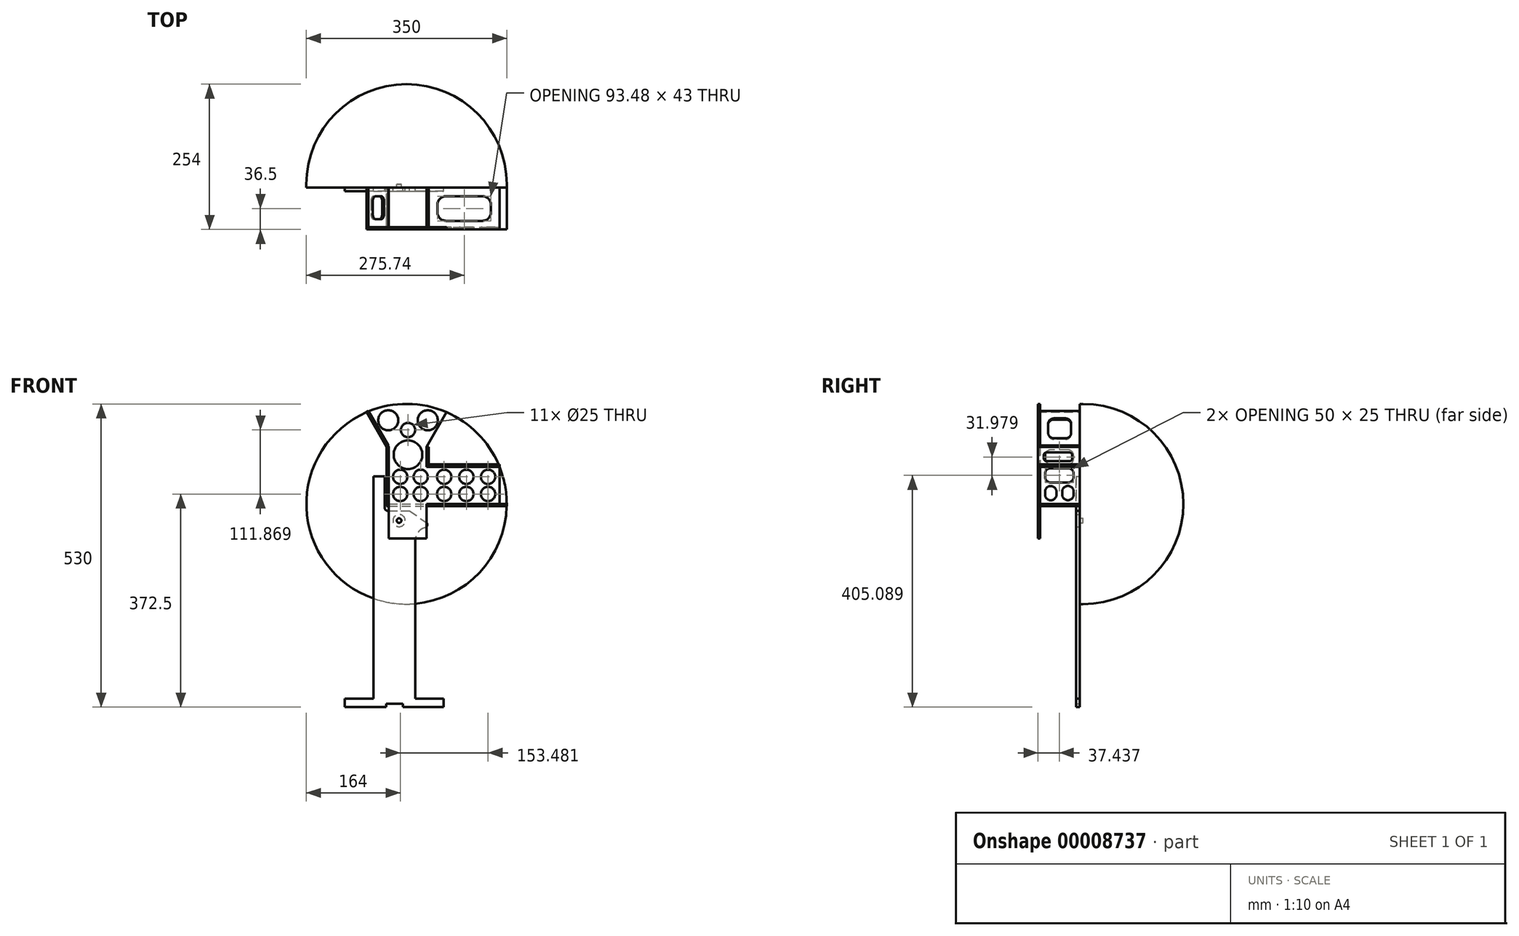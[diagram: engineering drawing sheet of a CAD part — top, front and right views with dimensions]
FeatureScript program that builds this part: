
annotation { "Feature Type Name" : "Feature", "Feature Type Description" : "" }
export const myFeature = defineFeature(function(context is Context, id is Id, definition is map)
    precondition{}
    {
        {
            var Q0;
            Q0=qCreatedBy(makeId("Right.planeOp"),FACE);
            cPlane(context, id + "F0", {"entities" : qUnion([Q0]), "cplaneType" : CPlaneType.OFFSET, "offset" : (70 / 2) * mm, "width" : 150 * mm, "height" : 150 * mm});
        }
        {
            var Q0;
            Q0=qCreatedBy(makeId("Front.planeOp"),FACE);
            var sketch = newSketch(context, id + "F1", { "sketchPlane" : qUnion([Q0])});
            skCircle(sketch, "E0", {"center": v(0, 0) * mm, "radius": 175 * mm});
            skCircle(sketch, "E1", {"center": v(-13, -29) * mm, "radius": 4 * mm});
            skSolve(sketch);
        }
        {
            var Q0;
            Q0 = qSketchRegion(id + "F1", true);
            extrude(context, id + "F2", {"entities" : qUnion([Q0]), "depth" : 6 * mm});
        }
        {
            var Q0;
            Q0=qCreatedBy(id+"F0.planeOp",FACE);
            var sketch = newSketch(context, id + "F3", { "sketchPlane" : qUnion([Q0])});
            skLineSegment(sketch, "E2.bottom", {"start": v(-6, 0) * mm, "end": v(-79, 0) * mm, "construction": true});
            skLineSegment(sketch, "E2.top", {"start": v(-6, 100) * mm, "end": v(-79, 100) * mm});
            skLineSegment(sketch, "E3", {"start": v(-79, 65) * mm, "end": v(-6, 65) * mm});
            skLineSegment(sketch, "E4", {"start": v(-79, 65) * mm, "end": v(-79, 0) * mm, "construction": true});
            skLineSegment(sketch, "E5", {"start": v(-79, 65) * mm, "end": v(-79, 100) * mm});
            skLineSegment(sketch, "E6", {"start": v(-6, 100) * mm, "end": v(-6, 65) * mm});
            skLineSegment(sketch, "E7", {"start": v(-6, 65) * mm, "end": v(-6, 0) * mm, "construction": true});
            skLineSegment(sketch, "E8.bottom", {"start": v(-64, 90) * mm, "end": v(-24, 90) * mm});
            skLineSegment(sketch, "E8.top", {"start": v(-64, 75) * mm, "end": v(-24, 75) * mm});
            skLineSegment(sketch, "E8.left", {"start": v(-69, 85) * mm, "end": v(-69, 80) * mm});
            skLineSegment(sketch, "E8.right", {"start": v(-19, 85) * mm, "end": v(-19, 80) * mm});
            skPoint(sketch, "E9.visualSharp", {"position": v(-69, 90) * mm});
            skArc(sketch, "E9.filletArc", {"start": v(-64, 90) * mm, "mid": v(-67.54, 88.54) * mm, "end": v(-69, 85) * mm});
            skPoint(sketch, "E10.visualSharp", {"position": v(-19, 90) * mm});
            skArc(sketch, "E10.filletArc", {"start": v(-19, 85) * mm, "mid": v(-20.46, 88.54) * mm, "end": v(-24, 90) * mm});
            skPoint(sketch, "E11.visualSharp", {"position": v(-19, 75) * mm});
            skArc(sketch, "E11.filletArc", {"start": v(-24, 75) * mm, "mid": v(-20.46, 76.46) * mm, "end": v(-19, 80) * mm});
            skPoint(sketch, "E12.visualSharp", {"position": v(-69, 75) * mm});
            skArc(sketch, "E12.filletArc", {"start": v(-69, 80) * mm, "mid": v(-67.54, 76.46) * mm, "end": v(-64, 75) * mm});
            skSolve(sketch);
        }
        {
            var Q0;
            Q0 = qSketchRegion(id + "F3", true);
            extrude(context, id + "F4", {"entities" : qUnion([Q0]), "depth" : 4 * mm});
        }
        {
            var Q0;
            Q0=qCreatedBy(makeId("Top.planeOp"),FACE);
            var sketch = newSketch(context, id + "F5", { "sketchPlane" : qUnion([Q0])});
            skLineSegment(sketch, "E13.bottom", {"start": v(175, -79) * mm, "end": v(35, -79) * mm});
            skLineSegment(sketch, "E13.top", {"start": v(175, -6) * mm, "end": v(-35, -6) * mm});
            skLineSegment(sketch, "E13.left", {"start": v(175, -79) * mm, "end": v(175, -6) * mm});
            skLineSegment(sketch, "E13.right", {"start": v(-35, -79) * mm, "end": v(-35, -6) * mm});
            skLineSegment(sketch, "E14.top", {"start": v(-31, -75) * mm, "end": v(35, -75) * mm});
            skLineSegment(sketch, "E14.left", {"start": v(-31, -79) * mm, "end": v(-31, -75) * mm});
            skLineSegment(sketch, "E14.right", {"start": v(35, -79) * mm, "end": v(35, -75) * mm});
            skLineSegment(sketch, "E15.trimOffspring", {"start": v(-31, -79) * mm, "end": v(-35, -79) * mm});
            skSolve(sketch);
        }
        {
            var Q0;
            Q0=makeQuery(id+"F5.imprint","IMPRINT",FACE,{"disambiguationData":[TD([[makeQuery(id+"F5.imprint","IMPRINT",EDGE,{"derivedFrom":sQuery(id+"F5.wireOp",EDGE,"E13.bottom")}),-1.0]])]});
            extrude(context, id + "F6", {"entities" : qUnion([Q0]), "oppositeDirection" : true, "depth" : 4 * mm});
        }
        {
            var Q0;
            Q0=makeQuery(id+"F6.opExtrude","SWEPT_FACE",FACE,{"disambiguationData":[OSD([sQuery(id+"F5.wireOp",EDGE,"E13.right")])]});
            var sketch = newSketch(context, id + "F7", { "sketchPlane" : qUnion([Q0])});
            skLineSegment(sketch, "E16.bottom", {"start": v(6, 0) * mm, "end": v(79, 0) * mm});
            skLineSegment(sketch, "E16.top", {"start": v(6, 100) * mm, "end": v(79, 100) * mm});
            skLineSegment(sketch, "E16.left", {"start": v(6, 0) * mm, "end": v(6, 100) * mm});
            skLineSegment(sketch, "E16.right", {"start": v(79, 0) * mm, "end": v(79, 100) * mm});
            skLineSegment(sketch, "E17.bottom", {"start": v(26.56, 62.59) * mm, "end": v(56.56, 62.59) * mm});
            skLineSegment(sketch, "E17.top", {"start": v(26.56, 37.59) * mm, "end": v(56.56, 37.59) * mm});
            skLineSegment(sketch, "E17.left", {"start": v(16.56, 52.59) * mm, "end": v(16.56, 47.59) * mm});
            skLineSegment(sketch, "E17.right", {"start": v(66.56, 52.59) * mm, "end": v(66.56, 47.59) * mm});
            skLineSegment(sketch, "E18.bottom", {"start": v(26.56, 94.57) * mm, "end": v(56.56, 94.57) * mm});
            skLineSegment(sketch, "E18.top", {"start": v(26.56, 69.57) * mm, "end": v(56.56, 69.57) * mm});
            skLineSegment(sketch, "E18.left", {"start": v(16.56, 84.57) * mm, "end": v(16.56, 79.57) * mm});
            skLineSegment(sketch, "E18.right", {"start": v(66.56, 84.57) * mm, "end": v(66.56, 79.57) * mm});
            skLineSegment(sketch, "E19.bottom", {"start": v(26.56, 31.59) * mm, "end": v(26.56, 31.59) * mm});
            skLineSegment(sketch, "E19.top", {"start": v(26.56, 6.59) * mm, "end": v(26.56, 6.59) * mm});
            skLineSegment(sketch, "E19.left", {"start": v(16.56, 21.59) * mm, "end": v(16.56, 16.59) * mm});
            skLineSegment(sketch, "E19.right", {"start": v(36.56, 21.59) * mm, "end": v(36.56, 16.59) * mm});
            skLineSegment(sketch, "E20.bottom", {"start": v(56.56, 31.33) * mm, "end": v(56.56, 31.33) * mm});
            skLineSegment(sketch, "E20.top", {"start": v(56.56, 6.33) * mm, "end": v(56.56, 6.33) * mm});
            skLineSegment(sketch, "E20.left", {"start": v(46.56, 21.33) * mm, "end": v(46.56, 16.33) * mm});
            skLineSegment(sketch, "E20.right", {"start": v(66.56, 21.33) * mm, "end": v(66.56, 16.33) * mm});
            skPoint(sketch, "E21.visualSharp", {"position": v(16.56, 94.57) * mm});
            skArc(sketch, "E21.filletArc", {"start": v(26.56, 94.57) * mm, "mid": v(19.5, 91.64) * mm, "end": v(16.56, 84.57) * mm});
            skPoint(sketch, "E22.visualSharp", {"position": v(66.56, 94.57) * mm});
            skArc(sketch, "E22.filletArc", {"start": v(66.56, 84.57) * mm, "mid": v(63.63, 91.64) * mm, "end": v(56.56, 94.57) * mm});
            skPoint(sketch, "E23.visualSharp", {"position": v(16.56, 69.57) * mm});
            skArc(sketch, "E23.filletArc", {"start": v(16.56, 79.57) * mm, "mid": v(19.5, 72.5) * mm, "end": v(26.56, 69.57) * mm});
            skPoint(sketch, "E24.visualSharp", {"position": v(66.56, 69.57) * mm});
            skArc(sketch, "E24.filletArc", {"start": v(56.56, 69.57) * mm, "mid": v(63.63, 72.5) * mm, "end": v(66.56, 79.57) * mm});
            skPoint(sketch, "E25.visualSharp", {"position": v(66.56, 62.59) * mm});
            skArc(sketch, "E25.filletArc", {"start": v(66.56, 52.59) * mm, "mid": v(63.63, 59.66) * mm, "end": v(56.56, 62.59) * mm});
            skPoint(sketch, "E26.visualSharp", {"position": v(16.56, 62.59) * mm});
            skArc(sketch, "E26.filletArc", {"start": v(26.56, 62.59) * mm, "mid": v(19.5, 59.66) * mm, "end": v(16.56, 52.59) * mm});
            skPoint(sketch, "E27.visualSharp", {"position": v(16.56, 37.59) * mm});
            skArc(sketch, "E27.filletArc", {"start": v(16.56, 47.59) * mm, "mid": v(19.5, 40.52) * mm, "end": v(26.56, 37.59) * mm});
            skPoint(sketch, "E28.visualSharp", {"position": v(66.56, 37.59) * mm});
            skArc(sketch, "E28.filletArc", {"start": v(56.56, 37.59) * mm, "mid": v(63.63, 40.52) * mm, "end": v(66.56, 47.59) * mm});
            skPoint(sketch, "E29.visualSharp", {"position": v(66.56, 31.33) * mm});
            skArc(sketch, "E29.filletArc", {"start": v(66.56, 21.33) * mm, "mid": v(63.63, 28.4) * mm, "end": v(56.56, 31.33) * mm});
            skPoint(sketch, "E30.visualSharp", {"position": v(46.56, 31.33) * mm});
            skArc(sketch, "E30.filletArc", {"start": v(56.56, 31.33) * mm, "mid": v(49.5, 28.4) * mm, "end": v(46.56, 21.33) * mm});
            skPoint(sketch, "E31.visualSharp", {"position": v(46.56, 6.33) * mm});
            skArc(sketch, "E31.filletArc", {"start": v(46.56, 16.33) * mm, "mid": v(49.5, 9.26) * mm, "end": v(56.56, 6.33) * mm});
            skPoint(sketch, "E32.visualSharp", {"position": v(66.56, 6.33) * mm});
            skArc(sketch, "E32.filletArc", {"start": v(56.56, 6.33) * mm, "mid": v(63.63, 9.26) * mm, "end": v(66.56, 16.33) * mm});
            skPoint(sketch, "E33.visualSharp", {"position": v(36.56, 31.59) * mm});
            skArc(sketch, "E33.filletArc", {"start": v(36.56, 21.59) * mm, "mid": v(33.63, 28.66) * mm, "end": v(26.56, 31.59) * mm});
            skPoint(sketch, "E34.visualSharp", {"position": v(16.56, 31.59) * mm});
            skArc(sketch, "E34.filletArc", {"start": v(26.56, 31.59) * mm, "mid": v(19.5, 28.66) * mm, "end": v(16.56, 21.59) * mm});
            skPoint(sketch, "E35.visualSharp", {"position": v(16.56, 6.59) * mm});
            skArc(sketch, "E35.filletArc", {"start": v(16.56, 16.59) * mm, "mid": v(19.5, 9.51) * mm, "end": v(26.56, 6.59) * mm});
            skPoint(sketch, "E36.visualSharp", {"position": v(36.56, 6.59) * mm});
            skArc(sketch, "E36.filletArc", {"start": v(26.56, 6.59) * mm, "mid": v(33.63, 9.51) * mm, "end": v(36.56, 16.59) * mm});
            skSolve(sketch);
        }
        {
            var Q0;
            Q0 = qSketchRegion(id + "F7", true);
            extrude(context, id + "F8", {"entities" : qUnion([Q0]), "oppositeDirection" : true, "depth" : 4 * mm});
        }
        {
            var Q0;
            Q0=makeQuery(id+"F6.opExtrude","SWEPT_FACE",FACE,{"disambiguationData":[OSD([sQuery(id+"F5.wireOp",EDGE,"E13.bottom")])]});
            var sketch = newSketch(context, id + "F9", { "sketchPlane" : qUnion([Q0])});
            skLineSegment(sketch, "E37", {"start": v(35, 100) * mm, "end": v(35, 65) * mm});
            skLineSegment(sketch, "E38", {"start": v(35, 65) * mm, "end": v(162.48, 65) * mm});
            skLineSegment(sketch, "E39", {"start": v(162.48, 65) * mm, "end": v(162.48, 0) * mm});
            skLineSegment(sketch, "E40", {"start": v(162.48, 0) * mm, "end": v(35, 0) * mm});
            skLineSegment(sketch, "E41", {"start": v(-31, 0) * mm, "end": v(-31, 100) * mm});
            skLineSegment(sketch, "E42", {"start": v(-31, 100) * mm, "end": v(-66.68, 161.8) * mm});
            skLineSegment(sketch, "E43", {"start": v(35, 100) * mm, "end": v(69.9, 160.44) * mm});
            skArc(sketch, "E44.0", {"start": v(69.9, 160.44) * mm, "mid": v(1.75, 175) * mm, "end": v(-66.68, 161.8) * mm});
            skLineSegment(sketch, "E45", {"start": v(-31, 0) * mm, "end": v(-31, -60) * mm});
            skLineSegment(sketch, "E46", {"start": v(-31, -60) * mm, "end": v(35, -60) * mm});
            skLineSegment(sketch, "E47", {"start": v(35, -60) * mm, "end": v(35, 0) * mm});
            skCircle(sketch, "E48", {"center": v(-13, -29) * mm, "radius": 4 * mm});
            skLineSegment(sketch, "E49", {"start": v(-11, 47.5) * mm, "end": v(142.48, 47.5) * mm, "construction": true});
            skLineSegment(sketch, "E50", {"start": v(142.48, 47.5) * mm, "end": v(142.48, 17.5) * mm, "construction": true});
            skLineSegment(sketch, "E51", {"start": v(142.48, 17.5) * mm, "end": v(-11, 17.5) * mm, "construction": true});
            skLineSegment(sketch, "E52", {"start": v(-11, 17.5) * mm, "end": v(-11, 47.5) * mm, "construction": true});
            skCircle(sketch, "E53", {"center": v(-11, 47.5) * mm, "radius": 12.5 * mm});
            skCircle(sketch, "E54", {"center": v(142.48, 47.5) * mm, "radius": 12.5 * mm});
            skCircle(sketch, "E55", {"center": v(142.48, 17.5) * mm, "radius": 12.5 * mm});
            skCircle(sketch, "E56", {"center": v(-11, 17.5) * mm, "radius": 12.5 * mm});
            skCircle(sketch, "E57", {"center": v(65.74, 47.5) * mm, "radius": 12.5 * mm});
            skCircle(sketch, "E58", {"center": v(65.74, 17.5) * mm, "radius": 12.5 * mm});
            skCircle(sketch, "E59", {"center": v(104.49, 47.5) * mm, "radius": 12.5 * mm});
            skCircle(sketch, "E60", {"center": v(24.7, 47.5) * mm, "radius": 12.5 * mm});
            skCircle(sketch, "E61", {"center": v(24.7, 17.5) * mm, "radius": 12.5 * mm});
            skCircle(sketch, "E62", {"center": v(104.49, 17.5) * mm, "radius": 12.5 * mm});
            skCircle(sketch, "E63", {"center": v(2.6, 86.17) * mm, "radius": 25 * mm});
            skCircle(sketch, "E64", {"center": v(-31.9, 146.32) * mm, "radius": 17.5 * mm});
            skCircle(sketch, "E65", {"center": v(37.1, 146.32) * mm, "radius": 17.5 * mm});
            skLineSegment(sketch, "E66", {"start": v(-31.9, 146.32) * mm, "end": v(37.1, 146.32) * mm, "construction": true});
            skLineSegment(sketch, "E67", {"start": v(2.6, 146.32) * mm, "end": v(2.6, 86.17) * mm, "construction": true});
            skCircle(sketch, "E68", {"center": v(2.6, 129.37) * mm, "radius": 12.5 * mm});
            skSolve(sketch);
        }
        {
            var Q0;
            Q0 = qSketchRegion(id + "F9", true);
            extrude(context, id + "F10", {"entities" : qUnion([Q0]), "oppositeDirection" : true, "depth" : 4 * mm});
        }
        {
            var Q0;
            Q0=makeQuery(id+"F2.opExtrude","CAP_FACE",FACE,{"disambiguationData":[OSD([sQuery(id+"F1.wireOp",EDGE,"E0")])],"isStart":false});
            var sketch = newSketch(context, id + "F11", { "sketchPlane" : qUnion([Q0])});
            skLineSegment(sketch, "E69", {"start": v(-35, 100) * mm, "end": v(-69.9, 160.44) * mm, "construction": true});
            skSolve(sketch);
        }
        {
            var Q0;
            Q0=sQuery(id+"F11.wireOp",VERTEX,"E69.end");
            var Q1;
            Q1=sQuery(id+"F11.wireOp",VERTEX,"E69.start");
            var Q2;
            Q2=makeQuery(id+"F8.opExtrude","CAP_VERTEX",VERTEX,{"disambiguationData":[OSD([sQuery(id+"F7.wireOp",EDGE,"E16.top"),sQuery(id+"F7.wireOp",EDGE,"E16.right")])],"isStart":true});
            cPlane(context, id + "F12", {"entities" : qUnion([Q0, Q1, Q2]), "cplaneType" : CPlaneType.THREE_POINT, "offset" : 150 * mm, "width" : 150 * mm, "height" : 150 * mm});
        }
        {
            var Q0;
            Q0=qCreatedBy(id+"F12.planeOp",FACE);
            var sketch = newSketch(context, id + "F13", { "sketchPlane" : qUnion([Q0])});
            skLineSegment(sketch, "E70.bottom", {"start": v(-79, 104.1) * mm, "end": v(-6, 104.1) * mm});
            skLineSegment(sketch, "E70.top", {"start": v(-79, 173.89) * mm, "end": v(-6, 173.89) * mm});
            skLineSegment(sketch, "E70.left", {"start": v(-79, 104.1) * mm, "end": v(-79, 173.89) * mm});
            skLineSegment(sketch, "E70.right", {"start": v(-6, 104.1) * mm, "end": v(-6, 173.89) * mm});
            skLineSegment(sketch, "E71.bottom", {"start": v(-31, 159.1) * mm, "end": v(-51, 159.1) * mm});
            skLineSegment(sketch, "E71.top", {"start": v(-31, 119.1) * mm, "end": v(-51, 119.1) * mm});
            skLineSegment(sketch, "E71.left", {"start": v(-21, 149.1) * mm, "end": v(-21, 129.1) * mm});
            skLineSegment(sketch, "E71.right", {"start": v(-61, 149.1) * mm, "end": v(-61, 129.1) * mm});
            skPoint(sketch, "E72.visualSharp", {"position": v(-21, 159.1) * mm});
            skArc(sketch, "E72.filletArc", {"start": v(-21, 149.1) * mm, "mid": v(-23.93, 156.17) * mm, "end": v(-31, 159.1) * mm});
            skPoint(sketch, "E73.visualSharp", {"position": v(-61, 159.1) * mm});
            skArc(sketch, "E73.filletArc", {"start": v(-51, 159.1) * mm, "mid": v(-58.07, 156.17) * mm, "end": v(-61, 149.1) * mm});
            skPoint(sketch, "E74.visualSharp", {"position": v(-61, 119.1) * mm});
            skArc(sketch, "E74.filletArc", {"start": v(-61, 129.1) * mm, "mid": v(-58.07, 122.03) * mm, "end": v(-51, 119.1) * mm});
            skPoint(sketch, "E75.visualSharp", {"position": v(-21, 119.1) * mm});
            skArc(sketch, "E75.filletArc", {"start": v(-31, 119.1) * mm, "mid": v(-23.93, 122.03) * mm, "end": v(-21, 129.1) * mm});
            skSolve(sketch);
        }
        {
            var Q0;
            Q0 = qSketchRegion(id + "F13", true);
            extrude(context, id + "F14", {"entities" : qUnion([Q0]), "depth" : 4 * mm});
        }
        {
            var Q0;
            Q0=makeQuery(id+"F10.opExtrude","SWEPT_FACE",FACE,{"disambiguationData":[OSD([sQuery(id+"F9.wireOp",EDGE,"E38")])]});
            var sketch = newSketch(context, id + "F15", { "sketchPlane" : qUnion([Q0])});
            skLineSegment(sketch, "E76.bottom", {"start": v(162.48, -79) * mm, "end": v(39, -79) * mm});
            skLineSegment(sketch, "E76.top", {"start": v(162.48, -6) * mm, "end": v(39, -6) * mm});
            skLineSegment(sketch, "E76.left", {"start": v(162.48, -79) * mm, "end": v(162.48, -6) * mm});
            skLineSegment(sketch, "E76.right", {"start": v(39, -79) * mm, "end": v(39, -6) * mm});
            skLineSegment(sketch, "E77.bottom", {"start": v(69, -64) * mm, "end": v(132.48, -64) * mm});
            skLineSegment(sketch, "E77.top", {"start": v(69, -21) * mm, "end": v(132.48, -21) * mm});
            skLineSegment(sketch, "E77.left", {"start": v(54, -49) * mm, "end": v(54, -36) * mm});
            skLineSegment(sketch, "E77.right", {"start": v(147.48, -49) * mm, "end": v(147.48, -36) * mm});
            skPoint(sketch, "E78.visualSharp", {"position": v(54, -64) * mm});
            skArc(sketch, "E78.filletArc", {"start": v(54, -49) * mm, "mid": v(58.4, -59.6) * mm, "end": v(69, -64) * mm});
            skPoint(sketch, "E79.visualSharp", {"position": v(54, -21) * mm});
            skArc(sketch, "E79.filletArc", {"start": v(69, -21) * mm, "mid": v(58.4, -25.4) * mm, "end": v(54, -36) * mm});
            skPoint(sketch, "E80.visualSharp", {"position": v(147.48, -21) * mm});
            skArc(sketch, "E80.filletArc", {"start": v(147.48, -36) * mm, "mid": v(143.09, -25.4) * mm, "end": v(132.48, -21) * mm});
            skPoint(sketch, "E81.visualSharp", {"position": v(147.48, -64) * mm});
            skArc(sketch, "E81.filletArc", {"start": v(132.48, -64) * mm, "mid": v(143.09, -59.6) * mm, "end": v(147.48, -49) * mm});
            skSolve(sketch);
        }
        {
            var Q0;
            Q0 = qSketchRegion(id + "F15", true);
            extrude(context, id + "F16", {"entities" : qUnion([Q0]), "depth" : 4 * mm});
        }
        {
            var Q0;
            Q0=makeQuery(id+"F11.imprint","IMPRINT",FACE,{"disambiguationData":[TD([[makeQuery(id+"F11.imprint","IMPRINT",EDGE,{"derivedFrom":makeQuery(id+"F2.opExtrude","CAP_EDGE",EDGE,{"disambiguationData":[OSD([sQuery(id+"F1.wireOp",EDGE,"E0")])],"isStart":false})}),1.0]])]});
            var sketch = newSketch(context, id + "F17", { "sketchPlane" : qUnion([Q0])});
            skCircle(sketch, "E82", {"center": v(-13, -29) * mm, "radius": 10.75 * mm});
            skLineSegment(sketch, "E83.top", {"start": v(-58, -355) * mm, "end": v(-35.38, -355) * mm});
            skLineSegment(sketch, "E83.right", {"start": v(15, -64.48) * mm, "end": v(15, -340) * mm});
            skLineSegment(sketch, "E84", {"start": v(15, -355) * mm, "end": v(65, -355) * mm});
            skLineSegment(sketch, "E85", {"start": v(65, -355) * mm, "end": v(65, -340) * mm});
            skLineSegment(sketch, "E86", {"start": v(65, -340) * mm, "end": v(15, -340) * mm});
            skLineSegment(sketch, "E87", {"start": v(-58, 48.12) * mm, "end": v(-38, 48.12) * mm});
            skLineSegment(sketch, "E88", {"start": v(-38, 48.12) * mm, "end": v(-38, -6.88) * mm});
            skLineSegment(sketch, "E89.right", {"start": v(5.23, -11.88) * mm, "end": v(5.23, -41.57) * mm, "construction": true});
            skPoint(sketch, "E90.visualSharp", {"position": v(15, -49) * mm});
            skArc(sketch, "E90.filletArc", {"start": v(32.68, -41.05) * mm, "mid": v(19.92, -49.8) * mm, "end": v(15, -64.48) * mm});
            skCircle(sketch, "E91", {"center": v(-13, -29) * mm, "radius": 25.01 * mm, "construction": true});
            skLineSegment(sketch, "E92", {"start": v(-13, -29) * mm, "end": v(-12.21, -4) * mm, "construction": true});
            skLineSegment(sketch, "E93", {"start": v(-13, -29) * mm, "end": v(5.23, -11.88) * mm, "construction": true});
            skLineSegment(sketch, "E94", {"start": v(5.23, -11.88) * mm, "end": v(34.18, -32.15) * mm});
            skLineSegment(sketch, "E95", {"start": v(47.64, -41.57) * mm, "end": v(5.23, -41.57) * mm, "construction": true});
            skLineSegment(sketch, "E96.bottom", {"start": v(-58, -355) * mm, "end": v(-108, -355) * mm});
            skLineSegment(sketch, "E96.top", {"start": v(-58, -340) * mm, "end": v(-108, -340) * mm});
            skLineSegment(sketch, "E96.right", {"start": v(-108, -355) * mm, "end": v(-108, -340) * mm});
            skLineSegment(sketch, "E97.top", {"start": v(-35.38, -349) * mm, "end": v(-6.32, -349) * mm});
            skLineSegment(sketch, "E97.left", {"start": v(-35.38, -355) * mm, "end": v(-35.38, -349) * mm});
            skLineSegment(sketch, "E97.right", {"start": v(-6.32, -355) * mm, "end": v(-6.32, -349) * mm});
            skLineSegment(sketch, "E98.trimOffspring", {"start": v(-6.32, -355) * mm, "end": v(15, -355) * mm});
            skLineSegment(sketch, "E99", {"start": v(-33, -11.88) * mm, "end": v(5.23, -11.88) * mm});
            skPoint(sketch, "E100.visualSharp", {"position": v(47.64, -41.57) * mm});
            skArc(sketch, "E100.filletArc", {"start": v(32.68, -41.05) * mm, "mid": v(36.24, -37.07) * mm, "end": v(34.18, -32.15) * mm});
            skPoint(sketch, "E101.visualSharp", {"position": v(-38, -11.88) * mm});
            skArc(sketch, "E101.filletArc", {"start": v(-38, -6.88) * mm, "mid": v(-36.54, -10.41) * mm, "end": v(-33, -11.88) * mm});
            skLineSegment(sketch, "E102", {"start": v(-58, -340) * mm, "end": v(-58, 48.12) * mm});
            skSolve(sketch);
        }
        {
            var Q0;
            Q0 = qSketchRegion(id + "F17", true);
            extrude(context, id + "F18", {"entities" : qUnion([Q0]), "depth" : 6 * mm});
        }
        {
            var Q0;
            Q0=makeQuery(id+"F2.opExtrude","CAP_FACE",FACE,{"disambiguationData":[OSD([sQuery(id+"F1.wireOp",EDGE,"E0"),sQuery(id+"F1.wireOp",EDGE,"E1")])],"isStart":true});
            var sketch = newSketch(context, id + "F19", { "sketchPlane" : qUnion([Q0])});
            skLineSegment(sketch, "E103", {"start": v(-175, 0) * mm, "end": v(175, 0) * mm});
            skArc(sketch, "E104.0", {"start": v(175, 0) * mm, "mid": v(0, 175) * mm, "end": v(-175, 0) * mm});
            skSolve(sketch);
        }
        {
            var Q0;
            Q0 = qSketchRegion(id + "F19", true);
            var Q1;
            Q1=sQuery(id+"F19.wireOp",EDGE,"E103");
            revolve(context, id + "F20", {"operationType" : NewBodyOperationType.ADD, "entities" : qUnion([Q0]), "axis" : qUnion([Q1]), "revolveType" : RevolveType.ONE_DIRECTION, "angle" : 180 * degree});
        }
    });
